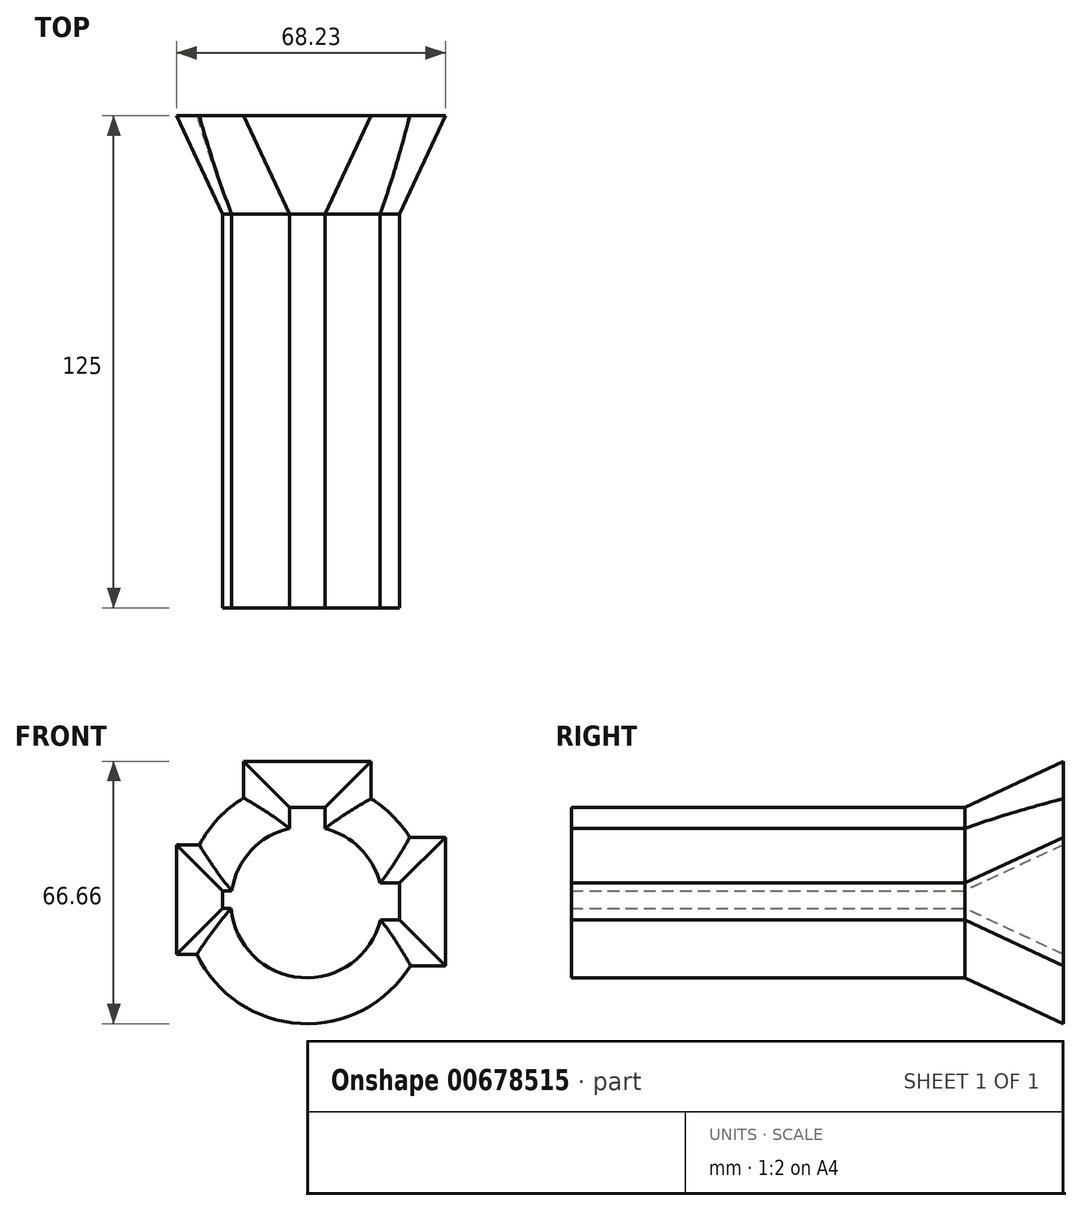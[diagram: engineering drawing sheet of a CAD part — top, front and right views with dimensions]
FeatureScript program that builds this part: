
annotation { "Feature Type Name" : "Feature", "Feature Type Description" : "" }
export const myFeature = defineFeature(function(context is Context, id is Id, definition is map)
    precondition{}
    {
        {
            var Q0;
            Q0=qCreatedBy(makeId("Front.planeOp"),FACE);
            var sketch = newSketch(context, id + "F0", { "sketchPlane" : qUnion([Q0])});
            skCircle(sketch, "E0", {"center": v(-0.44, -6.92) * mm, "radius": 19.25 * mm});
            skLineSegment(sketch, "E1.top", {"start": v(-4.81, 17.17) * mm, "end": v(4.22, 17.17) * mm});
            skLineSegment(sketch, "E1.left", {"start": v(-4.81, 11.82) * mm, "end": v(-4.81, 17.17) * mm});
            skLineSegment(sketch, "E1.right", {"start": v(4.22, 11.82) * mm, "end": v(4.22, 17.17) * mm});
            skLineSegment(sketch, "E2.bottom", {"start": v(18.2, -2.13) * mm, "end": v(23.14, -2.13) * mm});
            skLineSegment(sketch, "E2.top", {"start": v(18.2, -11.43) * mm, "end": v(23.14, -11.43) * mm});
            skLineSegment(sketch, "E2.right", {"start": v(23.14, -2.13) * mm, "end": v(23.14, -11.43) * mm});
            skLineSegment(sketch, "E3.bottom", {"start": v(-19.61, -8.57) * mm, "end": v(-21.78, -8.57) * mm});
            skLineSegment(sketch, "E3.top", {"start": v(-19.61, -4.05) * mm, "end": v(-21.78, -4.05) * mm});
            skLineSegment(sketch, "E3.right", {"start": v(-21.78, -8.57) * mm, "end": v(-21.78, -4.05) * mm});
            skLineSegment(sketch, "E4", {"start": v(-19.61, -4.05) * mm, "end": v(-19.47, -4.05) * mm});
            skLineSegment(sketch, "E5", {"start": v(4.22, 11.82) * mm, "end": v(4.22, 11.75) * mm});
            skSolve(sketch);
        }
        {
            var Q0;
            {var subQ0=sQuery(id+"F0.wireOp",EDGE,"E0");var subQ5=makeQuery(id+"F0.imprint","INTERSECT",VERTEX,{"derivedFrom":[subQ0,sQuery(id+"F0.wireOp",EDGE,"E2.bottom")]});Q0=makeQuery(id+"F0.imprint","IMPRINT",FACE,{"disambiguationData":[TD([[makeQuery(id+"F0.imprint","IMPRINT",EDGE,{"disambiguationData":[TD([[subQ5,-1.0]])],"derivedFrom":subQ0}),1.0]])]});}
            var Q1;
            Q1=makeQuery(id+"F0.imprint","IMPRINT",FACE,{"disambiguationData":[TD([[makeQuery(id+"F0.imprint","IMPRINT",EDGE,{"derivedFrom":sQuery(id+"F0.wireOp",EDGE,"E1.top")}),-1.0]])]});
            var Q2;
            {var subQ0=sQuery(id+"F0.wireOp",EDGE,"E3.bottom");Q2=makeQuery(id+"F0.imprint","IMPRINT",FACE,{"disambiguationData":[TD([[makeQuery(id+"F0.imprint","IMPRINT",EDGE,{"derivedFrom":subQ0}),-1.0]])]});}
            var Q3;
            {var subQ0=sQuery(id+"F0.wireOp",EDGE,"E2.bottom");Q3=makeQuery(id+"F0.imprint","IMPRINT",FACE,{"disambiguationData":[TD([[makeQuery(id+"F0.imprint","IMPRINT",EDGE,{"derivedFrom":subQ0}),-1.0]])]});}
            extrude(context, id + "F1", {"entities" : qUnion([Q0, Q1, Q2, Q3]), "depth" : 100 * mm, "offsetDistance" : 25 * mm});
        }
        {
            var Q0;
            Q0=makeQuery(id+"F1.opExtrude","CAP_FACE",FACE,{"disambiguationData":[OSD([sQuery(id+"F0.wireOp",EDGE,"E0"),sQuery(id+"F0.wireOp",EDGE,"E1.top"),sQuery(id+"F0.wireOp",EDGE,"E1.left"),sQuery(id+"F0.wireOp",EDGE,"E1.right"),sQuery(id+"F0.wireOp",EDGE,"E2.bottom"),sQuery(id+"F0.wireOp",EDGE,"E2.top"),sQuery(id+"F0.wireOp",EDGE,"E2.right"),sQuery(id+"F0.wireOp",EDGE,"E3.bottom"),sQuery(id+"F0.wireOp",EDGE,"E3.top"),sQuery(id+"F0.wireOp",EDGE,"E3.right"),sQuery(id+"F0.wireOp",EDGE,"E4"),sQuery(id+"F0.wireOp",EDGE,"E5")])],"isStart":true});
            extrude(context, id + "F2", {"entities" : qUnion([Q0]), "operationType" : NewBodyOperationType.ADD, "depth" : 25 * mm, "offsetDistance" : 25 * mm, "hasDraft" : true, "draftAngle" : 25 * degree});
        }
    });
